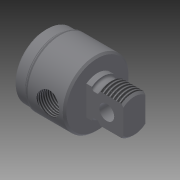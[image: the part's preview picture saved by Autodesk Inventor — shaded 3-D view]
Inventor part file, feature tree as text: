
AUTODESK INVENTOR PART (.ipt)
format: ipt  version: 2014 (Build 180170000, 170)  size: 290,816 bytes
history: native  units: in
note: dims shown in document units (in); Inventor stores cm internally (conversion verified against a paired STEP export)
features: other x154, sketch x7, revolve x4, thread x2, extrude x2, hole x1
ambient origin geometry x8: Origin, YZ Plane, XZ Plane, XY Plane, X Axis, Y Axis, Z Axis, Center Point
bodies: Solid1 (feature_tree)
feature tree (170):
  revolve  "Revolution1"  Angle=360.0deg
  revolve  "Revolution2"  [1 undecoded]
  thread  "Thread1"  [1 undecoded]
  extrude  "Extrusion1"  TaperAngle=360.0deg  [1 undecoded]
  hole  "Hole1"  [1 undecoded]
  revolve  "Revolution3"  [1 undecoded]
  thread  "Thread2"  [1 undecoded]
  revolve  "Revolution4"  [1 undecoded]
  extrude  "Extrusion2"  [1 undecoded]
  other  "1_XY"
  other  "1_YZ"
  other  "1_ZX"
  other  "1_X"
  other  "1_Y"
  other  "1_Z"
  other  "1_Center"
  other  "c1_XY"
  other  "c1_YZ"
  other  "c1_ZX"
  other  "c1_X"
  other  "c1_Y"
  other  "c1_Z"
  other  "c1_Center"
  other  "c2_XY"
  other  "c2_YZ"
  other  "c2_ZX"
  other  "c2_X"
  other  "c2_Y"
  other  "c2_Z"
  other  "c2_Center"
  other  "cc1_XY"
  other  "cc1_YZ"
  other  "cc1_ZX"
  other  "cc1_X"
  other  "cc1_Y"
  other  "cc1_Z"
  other  "cc1_Center"
  other  "cc2_XY"
  other  "cc2_YZ"
  other  "cc2_ZX"
  other  "cc2_X"
  other  "cc2_Y"
  other  "cc2_Z"
  other  "cc2_Center"
  other  "lovra1_XY"
  other  "lovra1_YZ"
  other  "lovra1_ZX"
  other  "lovra1_X"
  other  "lovra1_Y"
  other  "lovra1_Z"
  other  "lovra1_Center"
  other  "lovra2_XY"
  other  "lovra2_YZ"
  other  "lovra2_ZX"
  other  "lovra2_X"
  other  "lovra2_Y"
  other  "lovra2_Z"
  other  "lovra2_Center"
  other  "lovra21_XY"
  other  "lovra21_YZ"
  other  "lovra21_ZX"
  other  "lovra21_X"
  other  "lovra21_Y"
  other  "lovra21_Z"
  other  "lovra21_Center"
  other  "lovra22_XY"
  other  "lovra22_YZ"
  other  "lovra22_ZX"
  other  "lovra22_X"
  other  "lovra22_Y"
  other  "lovra22_Z"
  other  "lovra22_Center"
  other  "lovra3_XY"
  other  "lovra3_YZ"
  other  "lovra3_ZX"
  other  "lovra3_X"
  other  "lovra3_Y"
  other  "lovra3_Z"
  other  "lovra3_Center"
  other  "olen_XY"
  other  "olen_YZ"
  other  "olen_ZX"
  other  "olen_X"
  other  "olen_Y"
  other  "olen_Z"
  other  "olen_Center"
  other  "p1_XY"
  other  "p1_YZ"
  other  "p1_ZX"
  other  "p1_X"
  other  "p1_Y"
  other  "p1_Z"
  other  "p1_Center"
  other  "p2_XY"
  other  "p2_YZ"
  other  "p2_ZX"
  other  "p2_X"
  other  "p2_Y"
  other  "p2_Z"
  other  "p2_Center"
  other  "port_XY"
  other  "port_YZ"
  other  "port_ZX"
  other  "port_X"
  other  "port_Y"
  other  "port_Z"
  other  "port_Center"
  other  "port2_XY"
  other  "port2_YZ"
  other  "port2_ZX"
  other  "port2_X"
  other  "port2_Y"
  other  "port2_Z"
  other  "port2_Center"
  other  "thd1_XY"
  other  "thd1_YZ"
  other  "thd1_ZX"
  other  "thd1_X"
  other  "thd1_Y"
  other  "thd1_Z"
  other  "thd1_Center"
  other  "thd2_XY"
  other  "thd2_YZ"
  other  "thd2_ZX"
  other  "thd2_X"
  other  "thd2_Y"
  other  "thd2_Z"
  other  "thd2_Center"
  other  "to_mounting_bracket_XY"
  other  "to_mounting_bracket_YZ"
  other  "to_mounting_bracket_ZX"
  other  "to_mounting_bracket_X"
  other  "to_mounting_bracket_Y"
  other  "to_mounting_bracket_Z"
  other  "to_mounting_bracket_Center"
  other  "to_nut_XY"
  other  "to_nut_YZ"
  other  "to_nut_ZX"
  other  "to_nut_X"
  other  "to_nut_Y"
  other  "to_nut_Z"
  other  "to_nut_Center"
  other  "to_pin_XY"
  other  "to_pin_YZ"
  other  "to_pin_ZX"
  other  "to_pin_X"
  other  "to_pin_Y"
  other  "to_pin_Z"
  other  "to_pin_Center"
  other  "to_screw_XY"
  other  "to_screw_YZ"
  other  "to_screw_ZX"
  other  "to_screw_X"
  other  "to_screw_Y"
  other  "to_screw_Z"
  other  "to_screw_Center"
  other  "to_tube_XY"
  other  "to_tube_YZ"
  other  "to_tube_ZX"
  other  "to_tube_X"
  other  "to_tube_Y"
  other  "to_tube_Z"
  other  "to_tube_Center"
  sketch  "Sketch_18"  dims[d14=0.2731in d15=0.0in d16=360.0deg]
  sketch  "Sketch_15"  dims[d6=0.375in d7=0.75in d8=0.375in d9=0.25in d10=0.5635in d11=0.825in d12=120.0deg d13=360.0deg]
  sketch  "Sketch_9"  dims[d2=0.3547in d3=0.0in d4=0.625in d5=0.0in]
  sketch  "Sketch4"  dims[d0=360.0deg d1=360.0deg]
  sketch  "Sketch_68"
  sketch  "Sketch_24"  dims[d17=0.5587in d18=0.0in]
  sketch  "Sketch_43"
note: 8 required parameter values undecoded (feature->parameter linkage not recoverable at this tier; creation-order binding heuristic only, values carry confidence <= 0.55)